# Revit family: Urinal-Washdown-Sloan-Rear_Spud-SU-1219
name_source: partatom
category: Plumbing Fixtures
revit_build: Autodesk Revit 2014 (Build: 20130308_1515(x64)
units: mm (PartAtom-declared; Revit-internal decimal feet)

## types (1)
- SU-1219
    Assembly Code = D2010210
    CW Connection = Yes
    CWFU = 5
    Default Elevation = 17"
    Description = Complete HEU vitreous china retrofit rear spud urinal fixture.
    Fixture Color = Vitreous China-Sloan-White
    Flush Choice = Single Flush
    Flush Volumes and Flow Rates = 0.125 gpf to 0.5 gpf/0.5 Lpf to 1.9 Lpf
    HW Connection = No
    Inlet Spud Diameter = 3/4"
    Inlet Spud Size = 3/4” I.P.S. rear spud inlet
    Manufacturer = Sloan
    Model = SU-1219
    Mounting = Wall Hung
    Revised Date = 10/7/2016
    Spud Location = Rear Spud
    URL = http://www.sloan.com
    Vent Connection = No
    WFU = 5
    Waste Connection = Yes
    Waste Outlet Diameter = 2"

## geometry (parser evidence)
native form markers: Sweep x1
no freeform markers — native parametric forms only
